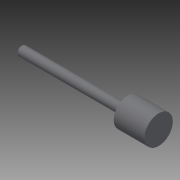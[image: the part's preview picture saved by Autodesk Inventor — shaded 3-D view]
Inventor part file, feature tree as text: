
AUTODESK INVENTOR PART (.ipt)
format: ipt  version: 2014 (Build 180170000, 170)  size: 117,248 bytes
history: native  units: in
note: dims shown in document units (in); Inventor stores cm internally (conversion verified against a paired STEP export)
features: other x49, revolve x2, sketch x2
ambient origin geometry x8: Origin, YZ Plane, XZ Plane, XY Plane, X Axis, Y Axis, Z Axis, Center Point
bodies: Solid1 (feature_tree)
feature tree (53):
  revolve  "Revolution1"  Angle=360.0deg
  revolve  "Revolution2"  [1 undecoded]
  other  "h1_XY"
  other  "h1_YZ"
  other  "h1_ZX"
  other  "h1_X"
  other  "h1_Y"
  other  "h1_Z"
  other  "h1_Center"
  other  "h2_XY"
  other  "h2_YZ"
  other  "h2_ZX"
  other  "h2_X"
  other  "h2_Y"
  other  "h2_Z"
  other  "h2_Center"
  other  "k1_XY"
  other  "k1_YZ"
  other  "k1_ZX"
  other  "k1_X"
  other  "k1_Y"
  other  "k1_Z"
  other  "k1_Center"
  other  "k2_XY"
  other  "k2_YZ"
  other  "k2_ZX"
  other  "k2_X"
  other  "k2_Y"
  other  "k2_Z"
  other  "k2_Center"
  other  "start_XY"
  other  "start_YZ"
  other  "start_ZX"
  other  "start_X"
  other  "start_Y"
  other  "start_Z"
  other  "start_Center"
  other  "to_prc_XY"
  other  "to_prc_YZ"
  other  "to_prc_ZX"
  other  "to_prc_X"
  other  "to_prc_Y"
  other  "to_prc_Z"
  other  "to_prc_Center"
  other  "to_rod_guide_XY"
  other  "to_rod_guide_YZ"
  other  "to_rod_guide_ZX"
  other  "to_rod_guide_X"
  other  "to_rod_guide_Y"
  other  "to_rod_guide_Z"
  other  "to_rod_guide_Center"
  sketch  "Sketch_5"  dims[d0=360.0deg d1=360.0deg]
  sketch  "Sketch_14"
note: 1 required parameter value undecoded (feature->parameter linkage not recoverable at this tier; creation-order binding heuristic only, values carry confidence <= 0.55)
